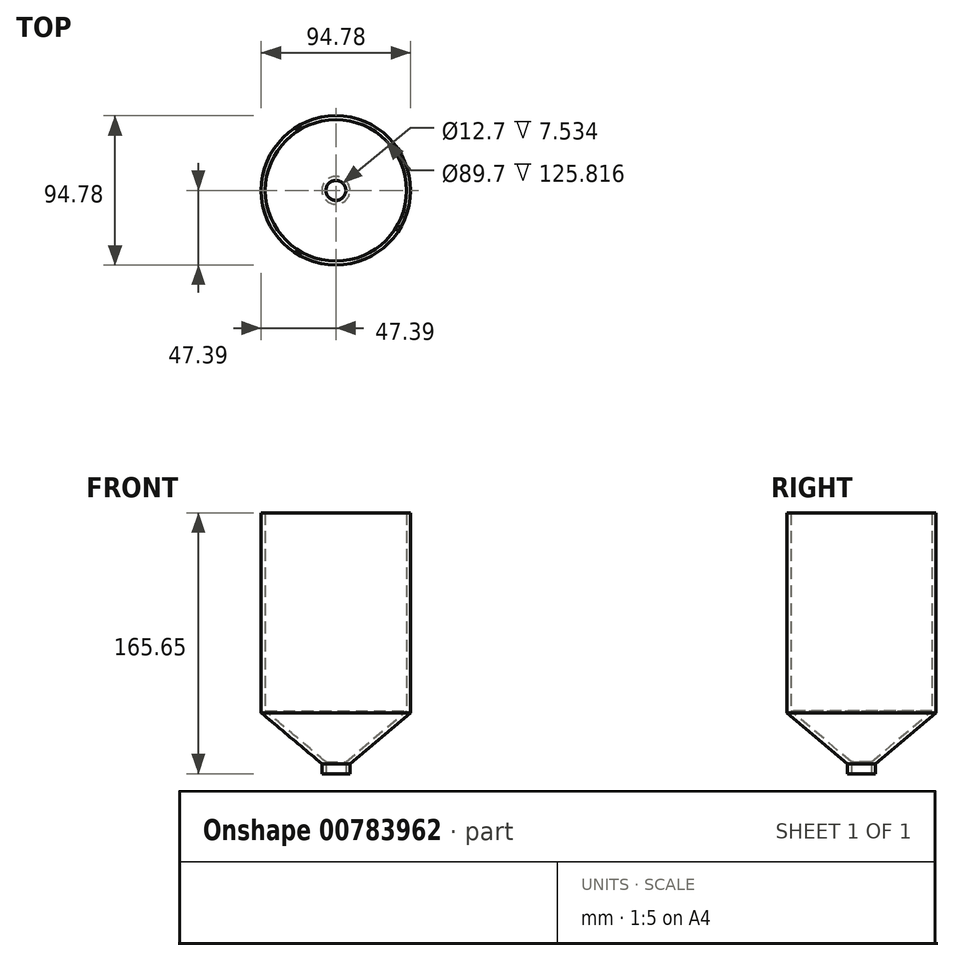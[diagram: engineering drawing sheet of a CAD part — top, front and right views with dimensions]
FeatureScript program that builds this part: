
annotation { "Feature Type Name" : "Feature", "Feature Type Description" : "" }
export const myFeature = defineFeature(function(context is Context, id is Id, definition is map)
    precondition{}
    {
        {
            var Q0;
            Q0=qCreatedBy(makeId("Right.planeOp"),FACE);
            var sketch = newSketch(context, id + "F0", { "sketchPlane" : qUnion([Q0])});
            skLineSegment(sketch, "E0", {"start": v(0, 0) * mm, "end": v(0, 23.87) * mm, "construction": true});
            skLineSegment(sketch, "E1", {"start": v(6.35, 0) * mm, "end": v(6.35, 7.53) * mm});
            skLineSegment(sketch, "E2", {"start": v(6.35, 7.53) * mm, "end": v(44.85, 39.84) * mm});
            skLineSegment(sketch, "E3", {"start": v(44.85, 39.84) * mm, "end": v(44.85, 165.65) * mm});
            skLineSegment(sketch, "E4", {"start": v(44.85, 165.65) * mm, "end": v(47.39, 165.65) * mm});
            skLineSegment(sketch, "E5", {"start": v(47.39, 165.65) * mm, "end": v(47.39, 38.65) * mm});
            skLineSegment(sketch, "E6", {"start": v(47.39, 38.65) * mm, "end": v(8.89, 6.35) * mm});
            skLineSegment(sketch, "E7", {"start": v(8.9, 6.35) * mm, "end": v(8.9, 0) * mm});
            skLineSegment(sketch, "E8", {"start": v(8.9, 0) * mm, "end": v(6.35, 0) * mm});
            skLineSegment(sketch, "E9", {"start": v(6.35, 0) * mm, "end": v(0, 0) * mm});
            skSolve(sketch);
        }
        {
            var Q0;
            Q0 = qSketchRegion(id + "F0", true);
            var Q1;
            Q1=sQuery(id+"F0.wireOp",EDGE,"E0");
            revolve(context, id + "F1", {"surfaceOperationType" : NewSurfaceOperationType.NEW, "entities" : qUnion([Q0]), "axis" : qUnion([Q1]), "revolveType" : RevolveType.FULL});
        }
    });
